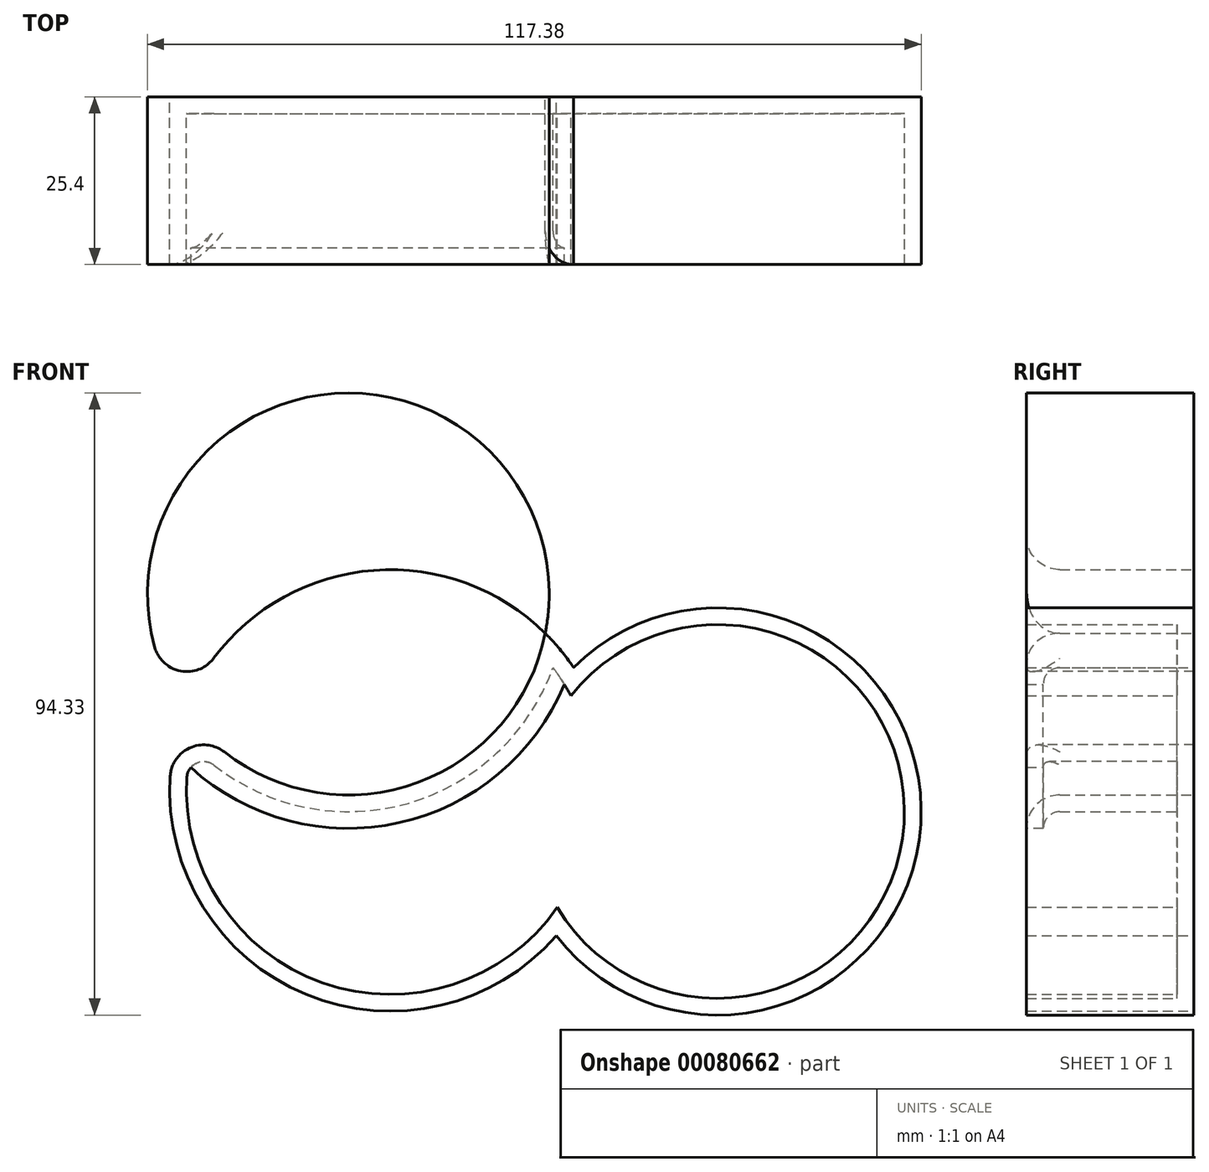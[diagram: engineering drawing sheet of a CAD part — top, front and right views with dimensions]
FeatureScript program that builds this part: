
annotation { "Feature Type Name" : "Feature", "Feature Type Description" : "" }
export const myFeature = defineFeature(function(context is Context, id is Id, definition is map)
    precondition{}
    {
        {
            var Q0;
            Q0=qCreatedBy(makeId("Front.planeOp"),FACE);
            var sketch = newSketch(context, id + "F0", { "sketchPlane" : qUnion([Q0])});
            skCircle(sketch, "E0", {"center": v(-35.38, 53.07) * mm, "radius": 30.47 * mm});
            skCircle(sketch, "E1", {"center": v(-119.25, 37.6) * mm, "radius": 1.64 * mm});
            skCircle(sketch, "E2", {"center": v(-29, 23.27) * mm, "radius": 33.47 * mm});
            skSolve(sketch);
        }
        {
            var Q0;
            {var subQ0=sQuery(id+"F0.wireOp",EDGE,"E2");var subQ1=sQuery(id+"F0.wireOp",EDGE,"E0");var subQ2=makeQuery(id+"F0.imprint","INTERSECT",VERTEX,{"disambiguationData":[OD(0.0)],"derivedFrom":[subQ1,subQ0]});Q0=makeQuery(id+"F0.imprint","IMPRINT",FACE,{"disambiguationData":[TD([[makeQuery(id+"F0.imprint","IMPRINT",EDGE,{"disambiguationData":[TD([[subQ2,1.0]])],"derivedFrom":subQ1}),1.0]])]});}
            var Q1;
            {var subQ0=sQuery(id+"F0.wireOp",EDGE,"E2");var subQ1=sQuery(id+"F0.wireOp",EDGE,"E0");var subQ2=makeQuery(id+"F0.imprint","INTERSECT",VERTEX,{"disambiguationData":[OD(0.0)],"derivedFrom":[subQ1,subQ0]});Q1=makeQuery(id+"F0.imprint","IMPRINT",FACE,{"disambiguationData":[TD([[makeQuery(id+"F0.imprint","IMPRINT",EDGE,{"disambiguationData":[TD([[subQ2,-1.0]])],"derivedFrom":subQ1}),-1.0]])]});}
            extrude(context, id + "F1", {"entities" : qUnion([Q0, Q1]), "depth" : 25.4 * mm});
        }
        {
            var Q0;
            Q0=qCreatedBy(makeId("Front.planeOp"),FACE);
            var sketch = newSketch(context, id + "F2", { "sketchPlane" : qUnion([Q0])});
            skCircle(sketch, "E3", {"center": v(20.65, 20.09) * mm, "radius": 30.88 * mm});
            skCircle(sketch, "E4", {"center": v(-164.54, 8.02) * mm, "radius": 3.9 * mm});
            skSolve(sketch);
        }
        {
            var Q0;
            Q0=makeQuery(id+"F2.imprint","IMPRINT",FACE,{"disambiguationData":[TD([[makeQuery(id+"F2.imprint","IMPRINT",EDGE,{"derivedFrom":sQuery(id+"F2.wireOp",EDGE,"E3")}),1.0]])]});
            extrude(context, id + "F3", {"entities" : qUnion([Q0]), "operationType" : NewBodyOperationType.ADD, "depth" : 25.4 * mm});
        }
        {
            var Q0;
            {var subQ0=sQuery(id+"F0.wireOp",EDGE,"E2");var subQ1=sQuery(id+"F0.wireOp",EDGE,"E0");var subQ2=makeQuery(id+"F0.imprint","INTERSECT",VERTEX,{"disambiguationData":[OD(0.0)],"derivedFrom":[subQ1,subQ0]});Q0=makeQuery(id+"F1.opExtrude","SWEPT_EDGE",EDGE,{"disambiguationData":[OSD([subQ1,subQ0]),TDD([subQ2]),ownerDisambiguation([makeQuery(id+"F1.opExtrude","SWEPT_BODY",BODY,{"disambiguationData":[OSD([subQ1,subQ0]),TDD([makeQuery(id+"F0.imprint","IMPRINT",EDGE,{"disambiguationData":[TD([[subQ2,-1.0]])],"derivedFrom":subQ1}),makeQuery(id+"F0.imprint","IMPRINT",EDGE,{"disambiguationData":[TD([[subQ2,-1.0]])],"derivedFrom":subQ0})])]})])]});}
            var Q1;
            {var subQ0=sQuery(id+"F0.wireOp",EDGE,"E2");var subQ1=sQuery(id+"F0.wireOp",EDGE,"E0");Q1=makeQuery(id+"F1.opExtrude","CAP_EDGE",EDGE,{"disambiguationData":[OSD([subQ1]),TDD([makeQuery(id+"F0.imprint","IMPRINT",EDGE,{"disambiguationData":[TD([[makeQuery(id+"F0.imprint","INTERSECT",VERTEX,{"disambiguationData":[OD(0.0)],"derivedFrom":[subQ1,subQ0]}),-1.0]])],"derivedFrom":subQ1})])],"isStart":false});}
            var Q2;
            {var subQ0=sQuery(id+"F0.wireOp",EDGE,"E2");var subQ1=sQuery(id+"F0.wireOp",EDGE,"E0");Q2=makeQuery(id+"F1.opExtrude","CAP_EDGE",EDGE,{"disambiguationData":[OSD([subQ0]),TDD([makeQuery(id+"F0.imprint","IMPRINT",EDGE,{"disambiguationData":[TD([[makeQuery(id+"F0.imprint","INTERSECT",VERTEX,{"disambiguationData":[OD(0.0)],"derivedFrom":[subQ1,subQ0]}),1.0]])],"derivedFrom":subQ0})])],"isStart":false});}
            fillet(context, id + "F4", {"entities" : qUnion([Q0, Q1, Q2]), "radius" : 5.08 * mm, "tangentPropagation" : true, "allowEdgeOverflow" : false});
        }
        {
            var Q0;
            {var subQ0=sQuery(id+"F0.wireOp",EDGE,"E2");var subQ1=sQuery(id+"F0.wireOp",EDGE,"E0");var subQ2=makeQuery(id+"F0.imprint","INTERSECT",VERTEX,{"disambiguationData":[OD(0.0)],"derivedFrom":[subQ1,subQ0]});Q0=makeQuery(id+"F3.boolean.opBoolean","MERGE",FACE,{"derivedFrom":[makeQuery(id+"F1.opExtrude","CAP_FACE",FACE,{"disambiguationData":[OSD([subQ1,subQ0]),TDD([makeQuery(id+"F0.imprint","IMPRINT",EDGE,{"disambiguationData":[TD([[subQ2,-1.0]])],"derivedFrom":subQ1}),makeQuery(id+"F0.imprint","IMPRINT",EDGE,{"disambiguationData":[TD([[subQ2,-1.0]])],"derivedFrom":subQ0})])],"isStart":false}),makeQuery(id+"F3.opExtrude","CAP_FACE",FACE,{"disambiguationData":[OSD([sQuery(id+"F2.wireOp",EDGE,"E3")])],"isStart":false})]});}
            shell(context, id + "F5", {"entities" : qUnion([Q0]), "thickness" : 2.54 * mm});
        }
    });
